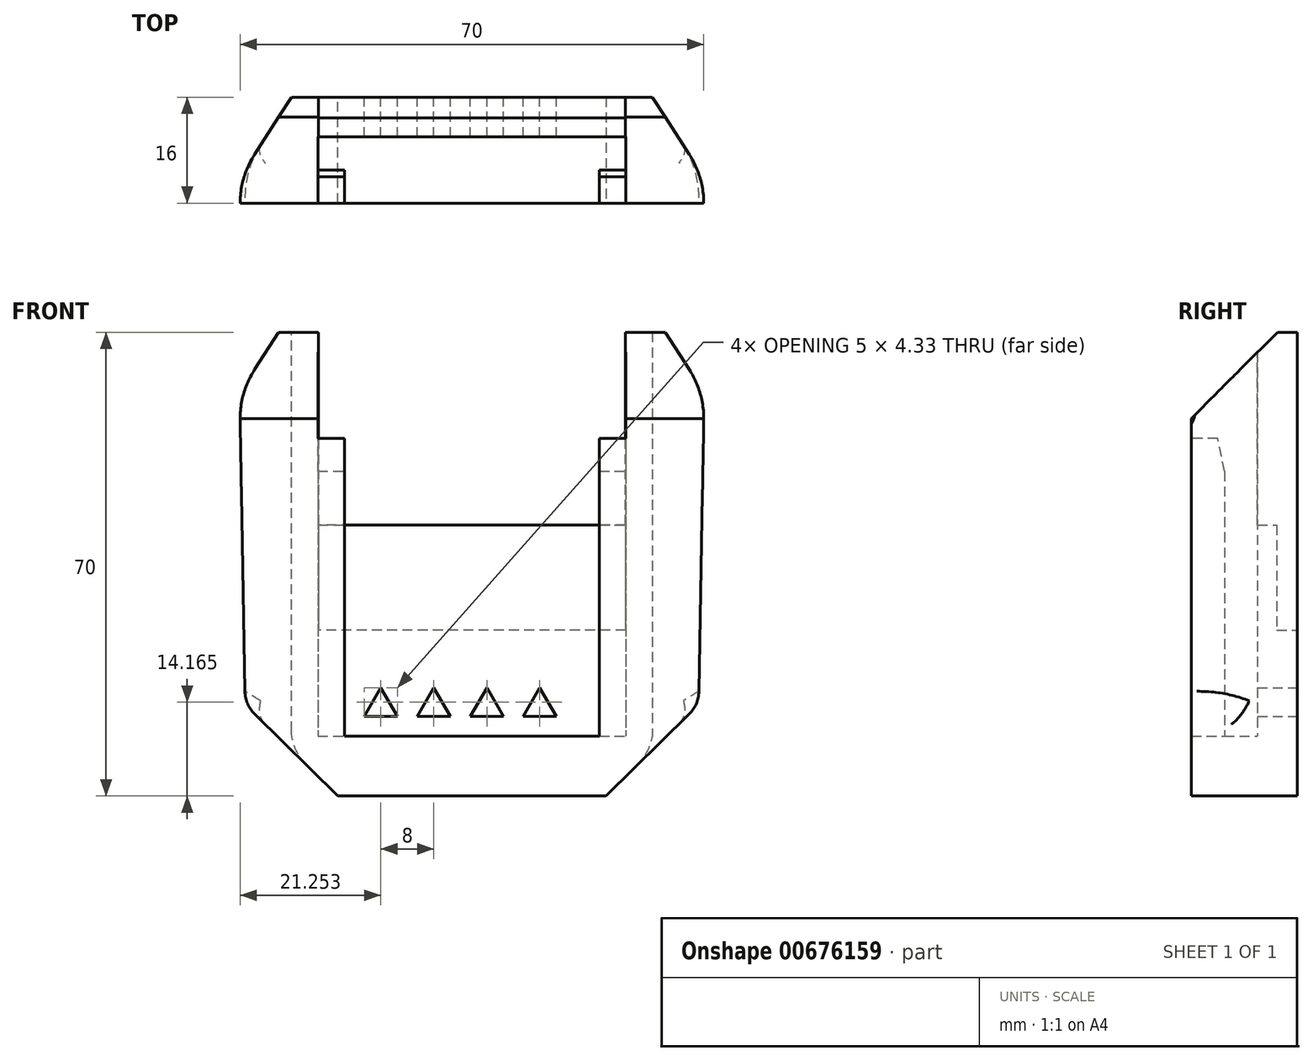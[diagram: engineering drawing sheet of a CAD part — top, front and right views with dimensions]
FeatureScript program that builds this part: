
annotation { "Feature Type Name" : "Feature", "Feature Type Description" : "" }
export const myFeature = defineFeature(function(context is Context, id is Id, definition is map)
    precondition{}
    {
        {
            var Q0;
            Q0=qCreatedBy(makeId("Top.planeOp"),FACE);
            var sketch = newSketch(context, id + "F0", { "sketchPlane" : qUnion([Q0])});
            skLineSegment(sketch, "E0", {"start": v(-23.79, 0) * mm, "end": v(-39.54, 0) * mm});
            skLineSegment(sketch, "E1", {"start": v(-39.54, 0) * mm, "end": v(-39.54, 16) * mm});
            skLineSegment(sketch, "E2", {"start": v(-39.54, 16) * mm, "end": v(30.46, 16) * mm});
            skLineSegment(sketch, "E3", {"start": v(30.46, 16) * mm, "end": v(30.46, 0) * mm});
            skLineSegment(sketch, "E4", {"start": v(30.46, 0) * mm, "end": v(14.71, 0) * mm});
            skLineSegment(sketch, "E5", {"start": v(14.71, 0) * mm, "end": v(14.71, 5) * mm});
            skLineSegment(sketch, "E6", {"start": v(14.71, 5) * mm, "end": v(18.71, 5) * mm});
            skLineSegment(sketch, "E7", {"start": v(18.71, 5) * mm, "end": v(18.71, 10) * mm});
            skLineSegment(sketch, "E8", {"start": v(18.71, 10) * mm, "end": v(-27.79, 10) * mm});
            skLineSegment(sketch, "E9", {"start": v(-27.79, 10) * mm, "end": v(-27.79, 5) * mm});
            skLineSegment(sketch, "E10", {"start": v(-27.79, 5) * mm, "end": v(-23.79, 5) * mm});
            skLineSegment(sketch, "E11", {"start": v(-23.79, 5) * mm, "end": v(-23.79, 0) * mm});
            skSolve(sketch);
        }
        {
            var Q0;
            Q0=makeQuery(id+"F0.imprint","IMPRINT",FACE,{"disambiguationData":[TD([[makeQuery(id+"F0.imprint","IMPRINT",EDGE,{"derivedFrom":sQuery(id+"F0.wireOp",EDGE,"E0")}),-1.0]])]});
            extrude(context, id + "F1", {"entities" : qUnion([Q0]), "depth" : 70 * mm, "offsetDistance" : 25 * mm});
        }
        {
            var Q0;
            Q0=makeQuery(id+"F1.opExtrude","SWEPT_EDGE",EDGE,{"disambiguationData":[OSD([sQuery(id+"F0.wireOp",EDGE,"E1"),sQuery(id+"F0.wireOp",EDGE,"E2")])]});
            var Q1;
            Q1=makeQuery(id+"F1.opExtrude","SWEPT_EDGE",EDGE,{"disambiguationData":[OSD([sQuery(id+"F0.wireOp",EDGE,"E2"),sQuery(id+"F0.wireOp",EDGE,"E3")])]});
            chamfer(context, id + "F2", {"entities" : qUnion([Q0, Q1]), "chamferType" : ChamferType.TWO_OFFSETS, "width1" : 12 * mm, "oppositeDirection" : false, "width2" : 7.75 * mm, "tangentPropagation" : true});
        }
        {
            var Q0;
            Q0=makeQuery(id+"F1.opExtrude","CAP_EDGE",EDGE,{"disambiguationData":[OSD([sQuery(id+"F0.wireOp",EDGE,"E0")])],"isStart":false});
            var Q1;
            Q1=makeQuery(id+"F1.opExtrude","CAP_EDGE",EDGE,{"disambiguationData":[OSD([sQuery(id+"F0.wireOp",EDGE,"E4")])],"isStart":false});
            chamfer(context, id + "F3", {"entities" : qUnion([Q0, Q1]), "width" : 13 * mm, "tangentPropagation" : true});
        }
        {
            var Q0;
            Q0=makeQuery(id+"F0.imprint","IMPRINT",FACE,{"disambiguationData":[TD([[makeQuery(id+"F0.imprint","IMPRINT",EDGE,{"derivedFrom":sQuery(id+"F0.wireOp",EDGE,"E0")}),-1.0]])]});
            cPlane(context, id + "F4", {"entities" : qUnion([Q0]), "cplaneType" : CPlaneType.OFFSET, "offset" : 70 * mm, "width" : 150 * mm, "height" : 150 * mm});
        }
        {
            var Q0;
            Q0=qCreatedBy(id+"F4.planeOp",FACE);
            var sketch = newSketch(context, id + "F5", { "sketchPlane" : qUnion([Q0])});
            skPoint(sketch, "E12.0", {"position": v(-27.79, 10) * mm});
            skPoint(sketch, "E13.0", {"position": v(18.71, 10) * mm});
            skLineSegment(sketch, "E14.0", {"start": v(30.46, 0) * mm, "end": v(14.71, 0) * mm});
            skLineSegment(sketch, "E15.0", {"start": v(-23.79, 0) * mm, "end": v(-39.54, 0) * mm});
            skLineSegment(sketch, "E16.bottom", {"start": v(-27.79, 10) * mm, "end": v(18.71, 10) * mm});
            skLineSegment(sketch, "E16.top", {"start": v(-27.79, 0) * mm, "end": v(18.71, 0) * mm});
            skLineSegment(sketch, "E16.left", {"start": v(-27.79, 10) * mm, "end": v(-27.79, 0) * mm});
            skLineSegment(sketch, "E16.right", {"start": v(18.71, 10) * mm, "end": v(18.71, 0) * mm});
            skSolve(sketch);
        }
        {
            var Q0;
            Q0=makeQuery(id+"F5.imprint","IMPRINT",FACE,{"disambiguationData":[TD([[makeQuery(id+"F5.imprint","IMPRINT",EDGE,{"derivedFrom":sQuery(id+"F5.wireOp",EDGE,"E16.bottom")}),-1.0]])]});
            extrude(context, id + "F6", {"entities" : qUnion([Q0]), "operationType" : NewBodyOperationType.REMOVE, "oppositeDirection" : true, "depth" : 16 * mm, "offsetDistance" : 25 * mm});
        }
        {
            var Q0;
            Q0=makeQuery(id+"F1.opExtrude","SWEPT_FACE",FACE,{"disambiguationData":[OSD([sQuery(id+"F0.wireOp",EDGE,"E2")])]});
            var sketch = newSketch(context, id + "F7", { "sketchPlane" : qUnion([Q0])});
            skLineSegment(sketch, "E17.bottom", {"start": v(-18.66, 70) * mm, "end": v(27.74, 70) * mm});
            skLineSegment(sketch, "E17.top", {"start": v(-18.66, 25) * mm, "end": v(27.74, 25) * mm});
            skLineSegment(sketch, "E17.left", {"start": v(-18.66, 70) * mm, "end": v(-18.66, 25) * mm});
            skLineSegment(sketch, "E17.right", {"start": v(27.74, 70) * mm, "end": v(27.74, 25) * mm});
            skLineSegment(sketch, "E18", {"start": v(27.74, 25) * mm, "end": v(31.79, 25) * mm, "construction": true});
            skLineSegment(sketch, "E19", {"start": v(-18.66, 25) * mm, "end": v(-22.71, 25) * mm, "construction": true});
            skSolve(sketch);
        }
        {
            var Q0;
            Q0=makeQuery(id+"F7.imprint","IMPRINT",FACE,{"disambiguationData":[TD([[makeQuery(id+"F7.imprint","IMPRINT",EDGE,{"derivedFrom":sQuery(id+"F7.wireOp",EDGE,"E17.bottom")}),1.0]])]});
            extrude(context, id + "F8", {"entities" : qUnion([Q0]), "operationType" : NewBodyOperationType.REMOVE, "oppositeDirection" : true, "depth" : 3.1 * mm, "offsetDistance" : 25 * mm});
        }
        {
            var Q0;
            Q0=makeQuery(id+"F8.boolean.opBoolean","COPY",FACE,{"derivedFrom":makeQuery(id+"F8.opExtrude","CAP_FACE",FACE,{"disambiguationData":[OSD([sQuery(id+"F7.wireOp",EDGE,"E17.bottom"),sQuery(id+"F7.wireOp",EDGE,"E17.top"),sQuery(id+"F7.wireOp",EDGE,"E17.left"),sQuery(id+"F7.wireOp",EDGE,"E17.right")])],"isStart":false})});
            var sketch = newSketch(context, id + "F9", { "sketchPlane" : qUnion([Q0])});
            skLineSegment(sketch, "E20.bottom", {"start": v(-18.66, 69.9) * mm, "end": v(27.74, 69.9) * mm});
            skLineSegment(sketch, "E20.top", {"start": v(-18.66, 40.9) * mm, "end": v(27.74, 40.9) * mm});
            skLineSegment(sketch, "E20.left", {"start": v(-18.66, 69.9) * mm, "end": v(-18.66, 40.9) * mm});
            skLineSegment(sketch, "E20.right", {"start": v(27.74, 69.9) * mm, "end": v(27.74, 40.9) * mm});
            skLineSegment(sketch, "E21.0.0", {"start": v(-18.66, 70) * mm, "end": v(-18.66, 25) * mm});
            skLineSegment(sketch, "E21.0.2", {"start": v(-18.66, 25) * mm, "end": v(-18.66, 70) * mm});
            skSolve(sketch);
        }
        {
            var Q0;
            {var subQ0=sQuery(id+"F9.wireOp",EDGE,"E20.top");Q0=makeQuery(id+"F9.imprint","IMPRINT",FACE,{"disambiguationData":[TD([[makeQuery(id+"F9.imprint","IMPRINT",EDGE,{"derivedFrom":subQ0}),1.0]])]});}
            extrude(context, id + "F10", {"entities" : qUnion([Q0]), "operationType" : NewBodyOperationType.REMOVE, "oppositeDirection" : true, "depth" : 3 * mm, "offsetDistance" : 25 * mm});
        }
        {
            var Q0;
            Q0=qCreatedBy(makeId("Top.planeOp"),FACE);
            var sketch = newSketch(context, id + "F11", { "sketchPlane" : qUnion([Q0])});
            skLineSegment(sketch, "E22.0.0", {"start": v(-23.79, 0) * mm, "end": v(-23.79, 5) * mm});
            skLineSegment(sketch, "E22.0.1", {"start": v(-23.79, 5) * mm, "end": v(-27.79, 5) * mm});
            skLineSegment(sketch, "E22.0.2", {"start": v(-27.79, 5) * mm, "end": v(-27.79, 10) * mm});
            skLineSegment(sketch, "E22.0.3", {"start": v(-27.79, 10) * mm, "end": v(18.71, 10) * mm});
            skLineSegment(sketch, "E22.0.4", {"start": v(18.71, 10) * mm, "end": v(18.71, 5) * mm});
            skLineSegment(sketch, "E22.0.5", {"start": v(18.71, 5) * mm, "end": v(14.71, 5) * mm});
            skLineSegment(sketch, "E22.0.6", {"start": v(14.71, 5) * mm, "end": v(14.71, 0) * mm});
            skLineSegment(sketch, "E22.0.7", {"start": v(14.71, 0) * mm, "end": v(30.46, 0) * mm});
            skLineSegment(sketch, "E22.0.8", {"start": v(30.46, 0) * mm, "end": v(30.46, 16) * mm});
            skLineSegment(sketch, "E22.0.9", {"start": v(30.46, 16) * mm, "end": v(-39.54, 16) * mm});
            skLineSegment(sketch, "E22.0.10", {"start": v(-39.54, 16) * mm, "end": v(-39.54, 0) * mm});
            skLineSegment(sketch, "E22.0.11", {"start": v(-39.54, 0) * mm, "end": v(-23.79, 0) * mm});
            skLineSegment(sketch, "E23.top", {"start": v(-27.79, 0) * mm, "end": v(18.71, 0) * mm});
            skLineSegment(sketch, "E23.left", {"start": v(-27.79, 10) * mm, "end": v(-27.79, 0) * mm});
            skLineSegment(sketch, "E23.right", {"start": v(18.71, 10) * mm, "end": v(18.71, 0) * mm});
            skSolve(sketch);
        }
        {
            var Q0;
            {var subQ5=sQuery(id+"F11.wireOp",EDGE,"E22.0.0");Q0=makeQuery(id+"F11.imprint","IMPRINT",FACE,{"disambiguationData":[TD([[makeQuery(id+"F11.imprint","IMPRINT",EDGE,{"derivedFrom":subQ5}),-1.0]])]});}
            extrude(context, id + "F12", {"entities" : qUnion([Q0]), "operationType" : NewBodyOperationType.ADD, "depth" : 9 * mm, "offsetDistance" : 25 * mm});
        }
        {
            var Q0;
            Q0=makeQuery(id+"F1.opExtrude","SWEPT_FACE",FACE,{"disambiguationData":[OSD([sQuery(id+"F0.wireOp",EDGE,"E2")])]});
            var sketch = newSketch(context, id + "F13", { "sketchPlane" : qUnion([Q0])});
            skCircle(sketch, "E24.cCircle", {"center": v(-5.71, 13.44) * mm, "radius": 1.44 * mm, "construction": true});
            skLineSegment(sketch, "E24.0", {"start": v(-3.21, 12) * mm, "end": v(-8.21, 12) * mm});
            skLineSegment(sketch, "E24.1", {"start": v(-8.21, 12) * mm, "end": v(-5.71, 16.33) * mm});
            skLineSegment(sketch, "E24.2", {"start": v(-5.71, 16.33) * mm, "end": v(-3.21, 12) * mm});
            skPoint(sketch, "E24.0.midPoint", {"position": v(-5.71, 12) * mm});
            skCircle(sketch, "E25.cCircle", {"center": v(2.29, 13.44) * mm, "radius": 1.44 * mm, "construction": true});
            skLineSegment(sketch, "E25.0", {"start": v(4.79, 12) * mm, "end": v(-0.21, 12) * mm});
            skLineSegment(sketch, "E25.1", {"start": v(-0.21, 12) * mm, "end": v(2.29, 16.33) * mm});
            skLineSegment(sketch, "E25.2", {"start": v(2.29, 16.33) * mm, "end": v(4.79, 12) * mm});
            skPoint(sketch, "E25.0.midPoint", {"position": v(2.29, 12) * mm});
            skCircle(sketch, "E26.cCircle", {"center": v(10.29, 13.44) * mm, "radius": 1.44 * mm, "construction": true});
            skLineSegment(sketch, "E26.0", {"start": v(12.79, 12) * mm, "end": v(7.79, 12) * mm});
            skLineSegment(sketch, "E26.1", {"start": v(7.79, 12) * mm, "end": v(10.29, 16.33) * mm});
            skLineSegment(sketch, "E26.2", {"start": v(10.29, 16.33) * mm, "end": v(12.79, 12) * mm});
            skPoint(sketch, "E26.0.midPoint", {"position": v(10.29, 12) * mm});
            skCircle(sketch, "E27.cCircle", {"center": v(18.29, 13.44) * mm, "radius": 1.44 * mm, "construction": true});
            skLineSegment(sketch, "E27.0", {"start": v(20.79, 12) * mm, "end": v(15.79, 12) * mm});
            skLineSegment(sketch, "E27.1", {"start": v(15.79, 12) * mm, "end": v(18.29, 16.33) * mm});
            skLineSegment(sketch, "E27.2", {"start": v(18.29, 16.33) * mm, "end": v(20.79, 12) * mm});
            skPoint(sketch, "E27.0.midPoint", {"position": v(18.29, 12) * mm});
            skSolve(sketch);
        }
        {
            var Q0;
            Q0=makeQuery(id+"F13.imprint","IMPRINT",FACE,{"disambiguationData":[TD([[makeQuery(id+"F13.imprint","IMPRINT",EDGE,{"derivedFrom":sQuery(id+"F13.wireOp",EDGE,"E24.0")}),-1.0]])]});
            var Q1;
            Q1=makeQuery(id+"F13.imprint","IMPRINT",FACE,{"disambiguationData":[TD([[makeQuery(id+"F13.imprint","IMPRINT",EDGE,{"derivedFrom":sQuery(id+"F13.wireOp",EDGE,"E25.0")}),-1.0]])]});
            var Q2;
            Q2=makeQuery(id+"F13.imprint","IMPRINT",FACE,{"disambiguationData":[TD([[makeQuery(id+"F13.imprint","IMPRINT",EDGE,{"derivedFrom":sQuery(id+"F13.wireOp",EDGE,"E26.0")}),-1.0]])]});
            var Q3;
            Q3=makeQuery(id+"F13.imprint","IMPRINT",FACE,{"disambiguationData":[TD([[makeQuery(id+"F13.imprint","IMPRINT",EDGE,{"derivedFrom":sQuery(id+"F13.wireOp",EDGE,"E27.0")}),-1.0]])]});
            extrude(context, id + "F14", {"entities" : qUnion([Q0, Q1, Q2, Q3]), "operationType" : NewBodyOperationType.REMOVE, "oppositeDirection" : true, "depth" : 25 * mm, "offsetDistance" : 25 * mm});
        }
        {
            var Q0;
            Q0=makeQuery(id+"F1.opExtrude","CAP_EDGE",EDGE,{"disambiguationData":[OSD([sQuery(id+"F0.wireOp",EDGE,"E3")])],"isStart":true});
            var Q1;
            Q1=makeQuery(id+"F1.opExtrude","CAP_EDGE",EDGE,{"disambiguationData":[OSD([sQuery(id+"F0.wireOp",EDGE,"E1")])],"isStart":true});
            chamfer(context, id + "F15", {"entities" : qUnion([Q0, Q1]), "chamferType" : ChamferType.TWO_OFFSETS, "width1" : 1 * mm, "oppositeDirection" : false, "width2" : 56 * mm, "tangentPropagation" : true});
        }
        {
            var Q0;
            {var subQ0=sQuery(id+"F0.wireOp",EDGE,"E3");Q0=makeQuery(id+"F15.opChamfer","BLEND_EDGE",EDGE,{"blendedFrom":[makeQuery(id+"F1.opExtrude","CAP_EDGE",EDGE,{"disambiguationData":[OSD([subQ0])],"isStart":true}),makeQuery(id+"F1.opExtrude","CAP_FACE",FACE,{"disambiguationData":[OSD([sQuery(id+"F0.wireOp",EDGE,"E0"),sQuery(id+"F0.wireOp",EDGE,"E1"),sQuery(id+"F0.wireOp",EDGE,"E2"),subQ0,sQuery(id+"F0.wireOp",EDGE,"E4"),sQuery(id+"F0.wireOp",EDGE,"E5"),sQuery(id+"F0.wireOp",EDGE,"E6"),sQuery(id+"F0.wireOp",EDGE,"E7"),sQuery(id+"F0.wireOp",EDGE,"E8"),sQuery(id+"F0.wireOp",EDGE,"E9"),sQuery(id+"F0.wireOp",EDGE,"E10"),sQuery(id+"F0.wireOp",EDGE,"E11")])],"isStart":true})],"blendedInto":[makeQuery(id+"F1.opExtrude","CAP_FACE",FACE,{"disambiguationData":[OSD([sQuery(id+"F0.wireOp",EDGE,"E0"),sQuery(id+"F0.wireOp",EDGE,"E1"),sQuery(id+"F0.wireOp",EDGE,"E2"),subQ0,sQuery(id+"F0.wireOp",EDGE,"E4"),sQuery(id+"F0.wireOp",EDGE,"E5"),sQuery(id+"F0.wireOp",EDGE,"E6"),sQuery(id+"F0.wireOp",EDGE,"E7"),sQuery(id+"F0.wireOp",EDGE,"E8"),sQuery(id+"F0.wireOp",EDGE,"E9"),sQuery(id+"F0.wireOp",EDGE,"E10"),sQuery(id+"F0.wireOp",EDGE,"E11")])],"isStart":true})]});}
            var Q1;
            {var subQ0=sQuery(id+"F0.wireOp",EDGE,"E1");Q1=makeQuery(id+"F15.opChamfer","BLEND_EDGE",EDGE,{"blendedFrom":[makeQuery(id+"F1.opExtrude","CAP_EDGE",EDGE,{"disambiguationData":[OSD([subQ0])],"isStart":true}),makeQuery(id+"F1.opExtrude","CAP_FACE",FACE,{"disambiguationData":[OSD([sQuery(id+"F0.wireOp",EDGE,"E0"),subQ0,sQuery(id+"F0.wireOp",EDGE,"E2"),sQuery(id+"F0.wireOp",EDGE,"E3"),sQuery(id+"F0.wireOp",EDGE,"E4"),sQuery(id+"F0.wireOp",EDGE,"E5"),sQuery(id+"F0.wireOp",EDGE,"E6"),sQuery(id+"F0.wireOp",EDGE,"E7"),sQuery(id+"F0.wireOp",EDGE,"E8"),sQuery(id+"F0.wireOp",EDGE,"E9"),sQuery(id+"F0.wireOp",EDGE,"E10"),sQuery(id+"F0.wireOp",EDGE,"E11")])],"isStart":true})],"blendedInto":[makeQuery(id+"F1.opExtrude","CAP_FACE",FACE,{"disambiguationData":[OSD([sQuery(id+"F0.wireOp",EDGE,"E0"),subQ0,sQuery(id+"F0.wireOp",EDGE,"E2"),sQuery(id+"F0.wireOp",EDGE,"E3"),sQuery(id+"F0.wireOp",EDGE,"E4"),sQuery(id+"F0.wireOp",EDGE,"E5"),sQuery(id+"F0.wireOp",EDGE,"E6"),sQuery(id+"F0.wireOp",EDGE,"E7"),sQuery(id+"F0.wireOp",EDGE,"E8"),sQuery(id+"F0.wireOp",EDGE,"E9"),sQuery(id+"F0.wireOp",EDGE,"E10"),sQuery(id+"F0.wireOp",EDGE,"E11")])],"isStart":true})]});}
            chamfer(context, id + "F16", {"entities" : qUnion([Q0, Q1]), "width" : 14 * mm, "tangentPropagation" : true});
        }
        {
            var Q0;
            {var subQ0=sQuery(id+"F0.wireOp",EDGE,"E3");Q0=makeQuery(id+"F15.opChamfer","BLEND_EDGE",EDGE,{"blendedFrom":[makeQuery(id+"F1.opExtrude","CAP_EDGE",EDGE,{"disambiguationData":[OSD([subQ0])],"isStart":true}),makeQuery(id+"F2.opChamfer","BLEND_FACE",FACE,{"disambiguationData":[OSD([sQuery(id+"F0.wireOp",EDGE,"E2"),subQ0])]})],"blendedInto":[makeQuery(id+"F2.opChamfer","BLEND_FACE",FACE,{"disambiguationData":[OSD([sQuery(id+"F0.wireOp",EDGE,"E2"),subQ0])]})]});}
            var Q1;
            {var subQ0=sQuery(id+"F0.wireOp",EDGE,"E1");Q1=makeQuery(id+"F15.opChamfer","BLEND_EDGE",EDGE,{"blendedFrom":[makeQuery(id+"F1.opExtrude","CAP_EDGE",EDGE,{"disambiguationData":[OSD([subQ0])],"isStart":true}),makeQuery(id+"F2.opChamfer","BLEND_FACE",FACE,{"disambiguationData":[OSD([subQ0,sQuery(id+"F0.wireOp",EDGE,"E2")])]})],"blendedInto":[makeQuery(id+"F2.opChamfer","BLEND_FACE",FACE,{"disambiguationData":[OSD([subQ0,sQuery(id+"F0.wireOp",EDGE,"E2")])]})]});}
            fillet(context, id + "F17", {"entities" : qUnion([Q0, Q1]), "radius" : 14.53 * mm, "tangentPropagation" : true, "allowEdgeOverflow" : false});
        }
        {
            var Q0;
            Q0=makeQuery(id+"F6.boolean.opBoolean","INTERSECT",EDGE,{"derivedFrom":[makeQuery(id+"F1.opExtrude","SWEPT_FACE",FACE,{"disambiguationData":[OSD([sQuery(id+"F0.wireOp",EDGE,"E10")])]}),makeQuery(id+"F6.opExtrude","CAP_FACE",FACE,{"disambiguationData":[OSD([sQuery(id+"F5.wireOp",EDGE,"E16.bottom"),sQuery(id+"F5.wireOp",EDGE,"E16.top"),sQuery(id+"F5.wireOp",EDGE,"E16.left"),sQuery(id+"F5.wireOp",EDGE,"E16.right")])],"isStart":false})]});
            var Q1;
            Q1=makeQuery(id+"F6.boolean.opBoolean","INTERSECT",EDGE,{"derivedFrom":[makeQuery(id+"F1.opExtrude","SWEPT_FACE",FACE,{"disambiguationData":[OSD([sQuery(id+"F0.wireOp",EDGE,"E6")])]}),makeQuery(id+"F6.opExtrude","CAP_FACE",FACE,{"disambiguationData":[OSD([sQuery(id+"F5.wireOp",EDGE,"E16.bottom"),sQuery(id+"F5.wireOp",EDGE,"E16.top"),sQuery(id+"F5.wireOp",EDGE,"E16.left"),sQuery(id+"F5.wireOp",EDGE,"E16.right")])],"isStart":false})]});
            chamfer(context, id + "F18", {"entities" : qUnion([Q0, Q1]), "chamferType" : ChamferType.TWO_OFFSETS, "width1" : 5 * mm, "oppositeDirection" : false, "width2" : 1 * mm, "tangentPropagation" : true});
        }
        {
            var Q0;
            {var subQ0=sQuery(id+"F11.wireOp",EDGE,"E23.right");var subQ1=sQuery(id+"F11.wireOp",EDGE,"E23.left");var subQ2=sQuery(id+"F11.wireOp",EDGE,"E23.top");var subQ3=sQuery(id+"F11.wireOp",EDGE,"E22.0.3");var subQ4=sQuery(id+"F11.wireOp",EDGE,"E22.0.6");var subQ5=sQuery(id+"F11.wireOp",EDGE,"E22.0.5");var subQ6=sQuery(id+"F11.wireOp",EDGE,"E22.0.1");var subQ7=sQuery(id+"F11.wireOp",EDGE,"E22.0.0");var subQ8=sQuery(id+"F0.wireOp",EDGE,"E11");var subQ9=sQuery(id+"F0.wireOp",EDGE,"E10");var subQ10=sQuery(id+"F0.wireOp",EDGE,"E9");var subQ11=sQuery(id+"F0.wireOp",EDGE,"E8");var subQ12=sQuery(id+"F0.wireOp",EDGE,"E7");var subQ13=sQuery(id+"F0.wireOp",EDGE,"E6");var subQ14=sQuery(id+"F0.wireOp",EDGE,"E5");var subQ15=sQuery(id+"F0.wireOp",EDGE,"E4");var subQ16=sQuery(id+"F0.wireOp",EDGE,"E3");var subQ17=sQuery(id+"F0.wireOp",EDGE,"E2");var subQ18=sQuery(id+"F0.wireOp",EDGE,"E1");var subQ19=sQuery(id+"F0.wireOp",EDGE,"E0");var subQ20=makeQuery(id+"F1.opExtrude","CAP_EDGE",EDGE,{"disambiguationData":[OSD([subQ16])],"isStart":true});Q0=makeQuery(id+"F17.opFillet","BLEND_EDGE",EDGE,{"blendedFrom":[makeQuery(id+"F15.opChamfer","BLEND_EDGE",EDGE,{"blendedFrom":[subQ20,makeQuery(id+"F2.opChamfer","BLEND_FACE",FACE,{"disambiguationData":[OSD([subQ17,subQ16])]})],"blendedInto":[makeQuery(id+"F2.opChamfer","BLEND_FACE",FACE,{"disambiguationData":[OSD([subQ17,subQ16])]})]}),makeQuery(id+"F16.opChamfer","BLEND_FACE",FACE,{"disambiguationData":[OSD([subQ19,subQ18,subQ17,subQ16,subQ15,subQ14,subQ13,subQ12,subQ11,subQ10,subQ9,subQ8,subQ7,subQ6,subQ5,subQ4,subQ3,subQ2,subQ1,subQ0]),TDD([makeQuery(id+"F15.opChamfer","BLEND_EDGE",EDGE,{"blendedFrom":[subQ20,makeQuery(id+"F12.boolean.opBoolean","MERGE",FACE,{"derivedFrom":[makeQuery(id+"F1.opExtrude","CAP_FACE",FACE,{"disambiguationData":[OSD([subQ19,subQ18,subQ17,subQ16,subQ15,subQ14,subQ13,subQ12,subQ11,subQ10,subQ9,subQ8])],"isStart":true}),makeQuery(id+"F12.opExtrude","CAP_FACE",FACE,{"disambiguationData":[OSD([subQ7,subQ6,subQ5,subQ4,subQ3,subQ2,subQ1,subQ0])],"isStart":true})]})],"blendedInto":[makeQuery(id+"F12.boolean.opBoolean","MERGE",FACE,{"derivedFrom":[makeQuery(id+"F1.opExtrude","CAP_FACE",FACE,{"disambiguationData":[OSD([subQ19,subQ18,subQ17,subQ16,subQ15,subQ14,subQ13,subQ12,subQ11,subQ10,subQ9,subQ8])],"isStart":true}),makeQuery(id+"F12.opExtrude","CAP_FACE",FACE,{"disambiguationData":[OSD([subQ7,subQ6,subQ5,subQ4,subQ3,subQ2,subQ1,subQ0])],"isStart":true})]})]})])]})],"blendedInto":[makeQuery(id+"F16.opChamfer","BLEND_FACE",FACE,{"disambiguationData":[OSD([subQ19,subQ18,subQ17,subQ16,subQ15,subQ14,subQ13,subQ12,subQ11,subQ10,subQ9,subQ8,subQ7,subQ6,subQ5,subQ4,subQ3,subQ2,subQ1,subQ0]),TDD([makeQuery(id+"F15.opChamfer","BLEND_EDGE",EDGE,{"blendedFrom":[subQ20,makeQuery(id+"F12.boolean.opBoolean","MERGE",FACE,{"derivedFrom":[makeQuery(id+"F1.opExtrude","CAP_FACE",FACE,{"disambiguationData":[OSD([subQ19,subQ18,subQ17,subQ16,subQ15,subQ14,subQ13,subQ12,subQ11,subQ10,subQ9,subQ8])],"isStart":true}),makeQuery(id+"F12.opExtrude","CAP_FACE",FACE,{"disambiguationData":[OSD([subQ7,subQ6,subQ5,subQ4,subQ3,subQ2,subQ1,subQ0])],"isStart":true})]})],"blendedInto":[makeQuery(id+"F12.boolean.opBoolean","MERGE",FACE,{"derivedFrom":[makeQuery(id+"F1.opExtrude","CAP_FACE",FACE,{"disambiguationData":[OSD([subQ19,subQ18,subQ17,subQ16,subQ15,subQ14,subQ13,subQ12,subQ11,subQ10,subQ9,subQ8])],"isStart":true}),makeQuery(id+"F12.opExtrude","CAP_FACE",FACE,{"disambiguationData":[OSD([subQ7,subQ6,subQ5,subQ4,subQ3,subQ2,subQ1,subQ0])],"isStart":true})]})]})])]})]});}
            var Q1;
            {var subQ0=sQuery(id+"F11.wireOp",EDGE,"E23.right");var subQ1=sQuery(id+"F11.wireOp",EDGE,"E23.left");var subQ2=sQuery(id+"F11.wireOp",EDGE,"E23.top");var subQ3=sQuery(id+"F11.wireOp",EDGE,"E22.0.3");var subQ4=sQuery(id+"F11.wireOp",EDGE,"E22.0.6");var subQ5=sQuery(id+"F11.wireOp",EDGE,"E22.0.5");var subQ6=sQuery(id+"F11.wireOp",EDGE,"E22.0.1");var subQ7=sQuery(id+"F11.wireOp",EDGE,"E22.0.0");var subQ8=sQuery(id+"F0.wireOp",EDGE,"E11");var subQ9=sQuery(id+"F0.wireOp",EDGE,"E10");var subQ10=sQuery(id+"F0.wireOp",EDGE,"E9");var subQ11=sQuery(id+"F0.wireOp",EDGE,"E8");var subQ12=sQuery(id+"F0.wireOp",EDGE,"E7");var subQ13=sQuery(id+"F0.wireOp",EDGE,"E6");var subQ14=sQuery(id+"F0.wireOp",EDGE,"E5");var subQ15=sQuery(id+"F0.wireOp",EDGE,"E4");var subQ16=sQuery(id+"F0.wireOp",EDGE,"E3");var subQ17=sQuery(id+"F0.wireOp",EDGE,"E2");var subQ18=sQuery(id+"F0.wireOp",EDGE,"E1");var subQ19=sQuery(id+"F0.wireOp",EDGE,"E0");var subQ20=makeQuery(id+"F1.opExtrude","CAP_EDGE",EDGE,{"disambiguationData":[OSD([subQ18])],"isStart":true});Q1=makeQuery(id+"F17.opFillet","BLEND_EDGE",EDGE,{"blendedFrom":[makeQuery(id+"F15.opChamfer","BLEND_EDGE",EDGE,{"blendedFrom":[subQ20,makeQuery(id+"F2.opChamfer","BLEND_FACE",FACE,{"disambiguationData":[OSD([subQ18,subQ17])]})],"blendedInto":[makeQuery(id+"F2.opChamfer","BLEND_FACE",FACE,{"disambiguationData":[OSD([subQ18,subQ17])]})]}),makeQuery(id+"F16.opChamfer","BLEND_FACE",FACE,{"disambiguationData":[OSD([subQ19,subQ18,subQ17,subQ16,subQ15,subQ14,subQ13,subQ12,subQ11,subQ10,subQ9,subQ8,subQ7,subQ6,subQ5,subQ4,subQ3,subQ2,subQ1,subQ0]),TDD([makeQuery(id+"F15.opChamfer","BLEND_EDGE",EDGE,{"blendedFrom":[subQ20,makeQuery(id+"F12.boolean.opBoolean","MERGE",FACE,{"derivedFrom":[makeQuery(id+"F1.opExtrude","CAP_FACE",FACE,{"disambiguationData":[OSD([subQ19,subQ18,subQ17,subQ16,subQ15,subQ14,subQ13,subQ12,subQ11,subQ10,subQ9,subQ8])],"isStart":true}),makeQuery(id+"F12.opExtrude","CAP_FACE",FACE,{"disambiguationData":[OSD([subQ7,subQ6,subQ5,subQ4,subQ3,subQ2,subQ1,subQ0])],"isStart":true})]})],"blendedInto":[makeQuery(id+"F12.boolean.opBoolean","MERGE",FACE,{"derivedFrom":[makeQuery(id+"F1.opExtrude","CAP_FACE",FACE,{"disambiguationData":[OSD([subQ19,subQ18,subQ17,subQ16,subQ15,subQ14,subQ13,subQ12,subQ11,subQ10,subQ9,subQ8])],"isStart":true}),makeQuery(id+"F12.opExtrude","CAP_FACE",FACE,{"disambiguationData":[OSD([subQ7,subQ6,subQ5,subQ4,subQ3,subQ2,subQ1,subQ0])],"isStart":true})]})]})])]})],"blendedInto":[makeQuery(id+"F16.opChamfer","BLEND_FACE",FACE,{"disambiguationData":[OSD([subQ19,subQ18,subQ17,subQ16,subQ15,subQ14,subQ13,subQ12,subQ11,subQ10,subQ9,subQ8,subQ7,subQ6,subQ5,subQ4,subQ3,subQ2,subQ1,subQ0]),TDD([makeQuery(id+"F15.opChamfer","BLEND_EDGE",EDGE,{"blendedFrom":[subQ20,makeQuery(id+"F12.boolean.opBoolean","MERGE",FACE,{"derivedFrom":[makeQuery(id+"F1.opExtrude","CAP_FACE",FACE,{"disambiguationData":[OSD([subQ19,subQ18,subQ17,subQ16,subQ15,subQ14,subQ13,subQ12,subQ11,subQ10,subQ9,subQ8])],"isStart":true}),makeQuery(id+"F12.opExtrude","CAP_FACE",FACE,{"disambiguationData":[OSD([subQ7,subQ6,subQ5,subQ4,subQ3,subQ2,subQ1,subQ0])],"isStart":true})]})],"blendedInto":[makeQuery(id+"F12.boolean.opBoolean","MERGE",FACE,{"derivedFrom":[makeQuery(id+"F1.opExtrude","CAP_FACE",FACE,{"disambiguationData":[OSD([subQ19,subQ18,subQ17,subQ16,subQ15,subQ14,subQ13,subQ12,subQ11,subQ10,subQ9,subQ8])],"isStart":true}),makeQuery(id+"F12.opExtrude","CAP_FACE",FACE,{"disambiguationData":[OSD([subQ7,subQ6,subQ5,subQ4,subQ3,subQ2,subQ1,subQ0])],"isStart":true})]})]})])]})]});}
            fillet(context, id + "F19", {"entities" : qUnion([Q0, Q1]), "radius" : 5 * mm, "tangentPropagation" : true, "allowEdgeOverflow" : false});
        }
    });
